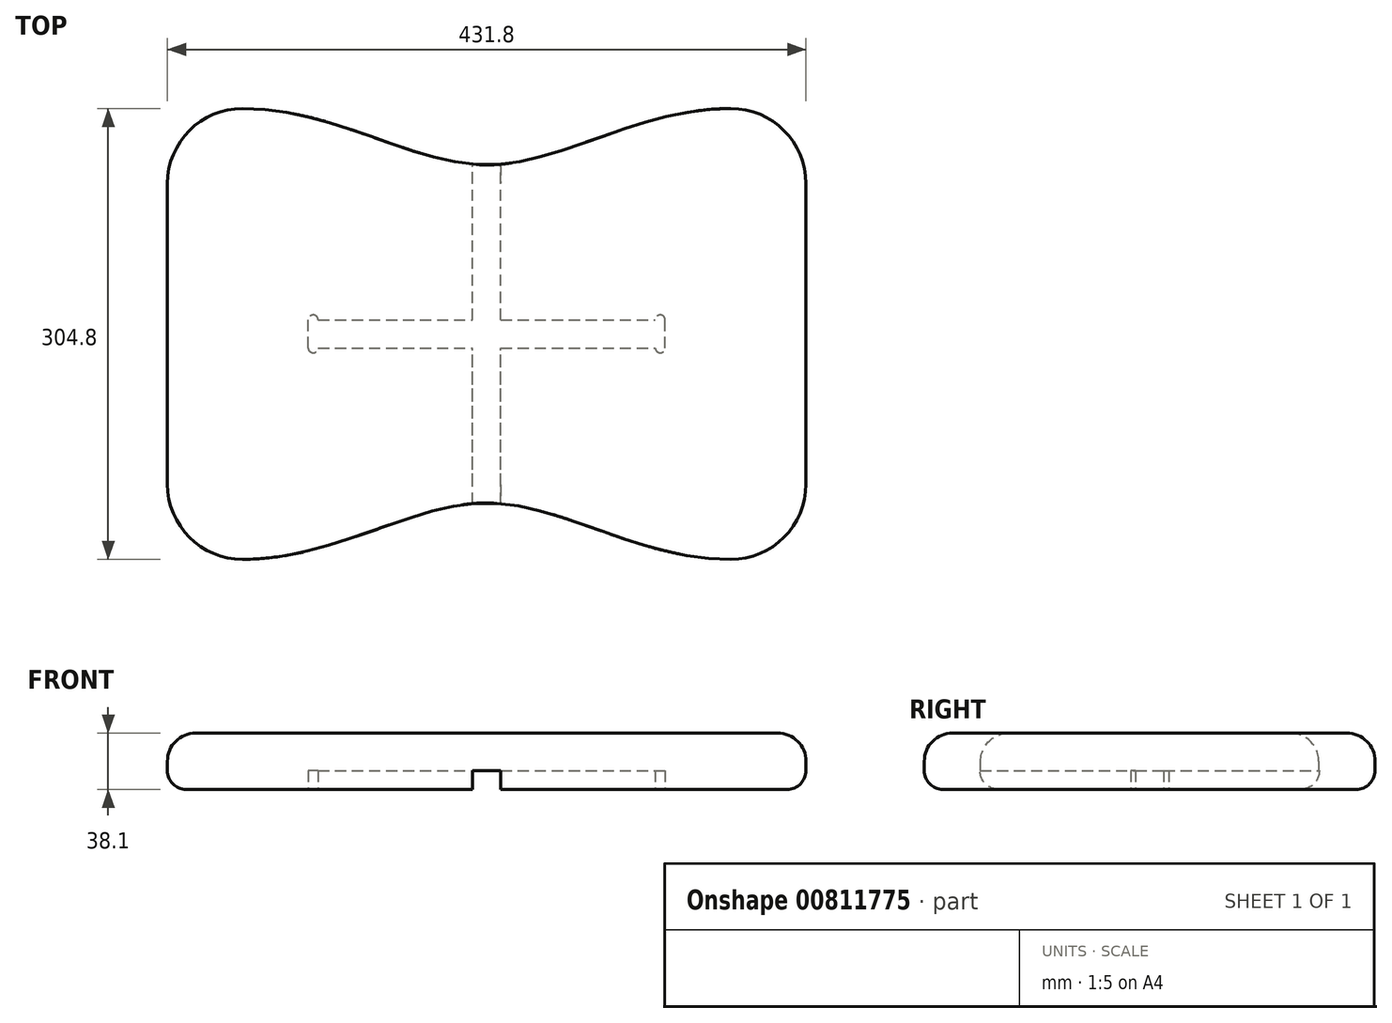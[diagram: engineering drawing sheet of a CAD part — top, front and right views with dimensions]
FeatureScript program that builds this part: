
annotation { "Feature Type Name" : "Feature", "Feature Type Description" : "" }
export const myFeature = defineFeature(function(context is Context, id is Id, definition is map)
    precondition{}
    {
        {
            var Q0;
            Q0=qCreatedBy(makeId("Top.planeOp"),FACE);
            var sketch = newSketch(context, id + "F0", { "sketchPlane" : qUnion([Q0])});
            skLineSegment(sketch, "E0.left", {"start": v(-215.9, 101.6) * mm, "end": v(-215.9, -101.6) * mm});
            skLineSegment(sketch, "E0.right", {"start": v(215.9, 101.6) * mm, "end": v(215.9, -101.6) * mm});
            skLineSegment(sketch, "E1", {"start": v(0, 152.4) * mm, "end": v(0, -152.4) * mm, "construction": true});
            skPoint(sketch, "E2.visualSharp", {"position": v(-215.9, 152.4) * mm});
            skArc(sketch, "E2.filletArc", {"start": v(-165.1, 152.4) * mm, "mid": v(-201.02, 137.52) * mm, "end": v(-215.9, 101.6) * mm});
            skPoint(sketch, "E3.visualSharp", {"position": v(-215.9, -152.4) * mm});
            skArc(sketch, "E3.filletArc", {"start": v(-215.9, -101.6) * mm, "mid": v(-201.02, -137.52) * mm, "end": v(-165.1, -152.4) * mm});
            skPoint(sketch, "E4.visualSharp", {"position": v(215.9, -152.4) * mm});
            skArc(sketch, "E4.filletArc", {"start": v(165.1, -152.4) * mm, "mid": v(201.02, -137.52) * mm, "end": v(215.9, -101.6) * mm});
            skPoint(sketch, "E5.visualSharp", {"position": v(215.9, 152.4) * mm});
            skArc(sketch, "E5.filletArc", {"start": v(215.9, 101.6) * mm, "mid": v(201.02, 137.52) * mm, "end": v(165.1, 152.4) * mm});
            skFitSpline(sketch, "E6", {"points": [v(-165.1, 152.4) * mm, v(0, 114.3) * mm, v(165.1, 152.4) * mm], "startDerivative": vector(381, 0) * mm, "endDerivative": vector(381, 0) * mm});
            skFitSpline(sketch, "E7", {"points": [v(-165.1, -152.4) * mm, v(0, -114.3) * mm, v(165.1, -152.4) * mm], "startDerivative": vector(381, 0) * mm, "endDerivative": vector(381, 0) * mm});
            skLineSegment(sketch, "E8", {"start": v(-215.9, 0) * mm, "end": v(215.9, 0) * mm, "construction": true});
            skSolve(sketch);
        }
        {
            var Q0;
            Q0=makeQuery(id+"F0.imprint","IMPRINT",FACE,{"disambiguationData":[TD([[makeQuery(id+"F0.imprint","IMPRINT",EDGE,{"derivedFrom":sQuery(id+"F0.wireOp",EDGE,"E0.left")}),1.0]])]});
            extrude(context, id + "F1", {"entities" : qUnion([Q0]), "depth" : 38.1 * mm, "offsetDistance" : 25.4 * mm});
        }
        {
            var Q0;
            Q0=makeQuery(id+"F1.opExtrude","CAP_FACE",FACE,{"disambiguationData":[OSD([sQuery(id+"F0.wireOp",EDGE,"E0.left"),sQuery(id+"F0.wireOp",EDGE,"E0.right"),sQuery(id+"F0.wireOp",EDGE,"E2.filletArc"),sQuery(id+"F0.wireOp",EDGE,"E3.filletArc"),sQuery(id+"F0.wireOp",EDGE,"E4.filletArc"),sQuery(id+"F0.wireOp",EDGE,"E5.filletArc"),sQuery(id+"F0.wireOp",EDGE,"E6"),sQuery(id+"F0.wireOp",EDGE,"E7")])],"isStart":true});
            var sketch = newSketch(context, id + "F2", { "sketchPlane" : qUnion([Q0])});
            skLineSegment(sketch, "E9.left", {"start": v(-120.65, 9.53) * mm, "end": v(-120.65, -9.53) * mm});
            skLineSegment(sketch, "E9.right", {"start": v(120.65, 9.53) * mm, "end": v(120.65, -9.52) * mm});
            skLineSegment(sketch, "E10.bottom", {"start": v(-9.53, 127) * mm, "end": v(9.52, 127) * mm});
            skLineSegment(sketch, "E10.top", {"start": v(-9.52, -127) * mm, "end": v(9.53, -127) * mm});
            skLineSegment(sketch, "E10.left", {"start": v(-9.53, 127) * mm, "end": v(-9.53, 9.52) * mm});
            skLineSegment(sketch, "E10.right", {"start": v(9.52, 127) * mm, "end": v(9.53, 9.53) * mm});
            skLineSegment(sketch, "E11", {"start": v(-120.65, 0) * mm, "end": v(120.65, 0) * mm, "construction": true});
            skLineSegment(sketch, "E12", {"start": v(0, 127) * mm, "end": v(0, -127) * mm, "construction": true});
            skLineSegment(sketch, "E13.trimOffspring", {"start": v(9.53, -9.53) * mm, "end": v(114.05, -9.53) * mm});
            skLineSegment(sketch, "E14.trimOffspring", {"start": v(-9.53, -9.52) * mm, "end": v(-9.52, -127) * mm});
            skLineSegment(sketch, "E15.trimOffspring", {"start": v(9.53, 9.53) * mm, "end": v(114.05, 9.53) * mm});
            skLineSegment(sketch, "E16.trimOffspring", {"start": v(9.53, -9.53) * mm, "end": v(9.53, -127) * mm});
            skArc(sketch, "E17", {"start": v(-120.65, -9.53) * mm, "mid": v(-117.35, -12.83) * mm, "end": v(-114.05, -9.53) * mm});
            skArc(sketch, "E18", {"start": v(-114.05, 9.52) * mm, "mid": v(-117.35, 12.83) * mm, "end": v(-120.65, 9.53) * mm});
            skArc(sketch, "E19", {"start": v(114.05, -9.52) * mm, "mid": v(117.35, -12.83) * mm, "end": v(120.65, -9.52) * mm});
            skArc(sketch, "E20", {"start": v(120.65, 9.53) * mm, "mid": v(117.35, 12.83) * mm, "end": v(114.05, 9.53) * mm});
            skLineSegment(sketch, "E21.trimOffspring", {"start": v(-114.05, 9.53) * mm, "end": v(-9.53, 9.53) * mm});
            skLineSegment(sketch, "E22.trimOffspring", {"start": v(-114.05, -9.53) * mm, "end": v(-9.53, -9.53) * mm});
            skSolve(sketch);
        }
        {
            var Q0;
            Q0=makeQuery(id+"F2.imprint","IMPRINT",FACE,{"disambiguationData":[TD([[makeQuery(id+"F2.imprint","IMPRINT",EDGE,{"derivedFrom":sQuery(id+"F2.wireOp",EDGE,"E9.left")}),1.0]])]});
            extrude(context, id + "F3", {"entities" : qUnion([Q0]), "operationType" : NewBodyOperationType.REMOVE, "oppositeDirection" : true, "depth" : 12.7 * mm, "offsetDistance" : 25.4 * mm});
        }
        {
            var Q0;
            Q0=makeQuery(id+"F1.opExtrude","CAP_EDGE",EDGE,{"disambiguationData":[OSD([sQuery(id+"F0.wireOp",EDGE,"E3.filletArc")])],"isStart":true});
            var Q1;
            {var subQ0=sQuery(id+"F0.wireOp",EDGE,"E7");var subQ1=sQuery(id+"F0.wireOp",EDGE,"E4.filletArc");Q1=makeQuery(id+"F3.boolean.opBoolean","SPLIT",EDGE,{"disambiguationData":[TD([makeQuery(id+"F1.opExtrude","SWEPT_FACE",FACE,{"disambiguationData":[OSD([subQ1])]})])],"derivedFrom":makeQuery(id+"F1.opExtrude","CAP_EDGE",EDGE,{"disambiguationData":[OSD([subQ0])],"isStart":true})});}
            fillet(context, id + "F4", {"entities" : qUnion([Q0, Q1]), "radius" : 12.7 * mm, "tangentPropagation" : true, "allowEdgeOverflow" : false});
        }
        {
            var Q0;
            Q0=makeQuery(id+"F1.opExtrude","CAP_EDGE",EDGE,{"disambiguationData":[OSD([sQuery(id+"F0.wireOp",EDGE,"E6")])],"isStart":false});
            fillet(context, id + "F5", {"entities" : qUnion([Q0]), "radius" : 19.05 * mm, "tangentPropagation" : true, "allowEdgeOverflow" : false});
        }
    });
